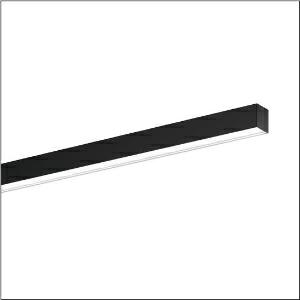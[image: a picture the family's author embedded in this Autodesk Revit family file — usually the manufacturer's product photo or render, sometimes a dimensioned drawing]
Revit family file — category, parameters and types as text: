
# Revit family: silica_r__21_51mx23db45bb_2d31
name_source: partatom
category: Lighting Fixtures
units: mm (PartAtom-declared; Revit-internal decimal feet)

## family parameters
Cut with Voids When Loaded = No
Host = Face
Light Source = No
Part Type = Normal
Room Calculation Point = No
Round Connector Dimension = Use Diameter
Shared = No

## types (1)
- --- (1 x LED, 4100 lm, 28.1 W, 4000K)
    Apparent Load = 28 VA
    CIE Flux Codes = 78 96 99 100 100
    Color Rendering = 80
    Color Temperature = 4000K
    Default Elevation = 1800 mm
    Description = Silica® 21, office luminaire, primary optical cover: prismatic diffuser, of PMMA, CAT 2 (L<= 3000cd/m²), light emission: direct distribution, primary light characteristic: symmetric, installation type: surface-mounted, LED, rated luminous flux: 4.100lm, luminous efficacy: 146lm/W, light colour: 840, colour temperature: 4000K, with terminal, 3+2-pole, max. 2.5mm², mains connection: 220..240V, AC, 50/60Hz, rated input power: 28.1W, luminaire housing, of aluminium, jet black (RAL 9005), length: 1.504mm, width: 53mm, height: 53mm, protection rating (complete): IP20, insulation class (complete): insulation class I (protective earthing), certification: CE, permissible operating ambient temperature: 0..+35°C, standard: EN 50419, packaging unit: 1 piece
    Height = 0 mm  [stored 0 ft]
    Lamp = 1 x LED
    Lamp Light Flux = 4100 lm
    Lamp Power = 28.1 W
    Lamp count = 1
    Length = 1504 mm
    Luminous efficacy = 146 lm/W
    Manufacturer = Siteco
    ModVariant = No
    Model = 51MX23DB45BB
    Mounting Place = Ceiling
    Mounting Type = Recessed
    Number of Poles = 1
    OnlyDefault = Yes
    Power Factor = 1
    Product Name = Silica® 21
    Product group = office luminaire | ceiling recessed
    ProductGroupID = 401
    Protection Class = Protection class I
    Protection Degree = IP 20
    RLX_Detail_Level = 1
    RLX_Emergency_Light_Flux = 0 lm
    RLX_Emergency_Type = 0
    RLX_Emergency_Type_DB = No
    RlxData = <blob elided: 23685 chars, md5=3488cca7>
    Socket = socket
    Standby Power = 0 W
    System Light Flux = 4100 lm
    System Power = 28 W
    Type Comments = factory setting: luminous flux: 100 % | dim-lin: 254 | 323 mA
    Type Image = l_1297760.jpg
    URL = http://relux.com
    VarID = @adj_049949
    Voltage = 0 V
    Weight = 0.00 kg
    Width = 53 mm

note: [stored X ft] marks values corroborated as IEEE doubles in the binary element streams (Revit-internal decimal feet)

## geometry (parser evidence)
native form markers: Blend x4, Sweep x11
no freeform markers — native parametric forms only
